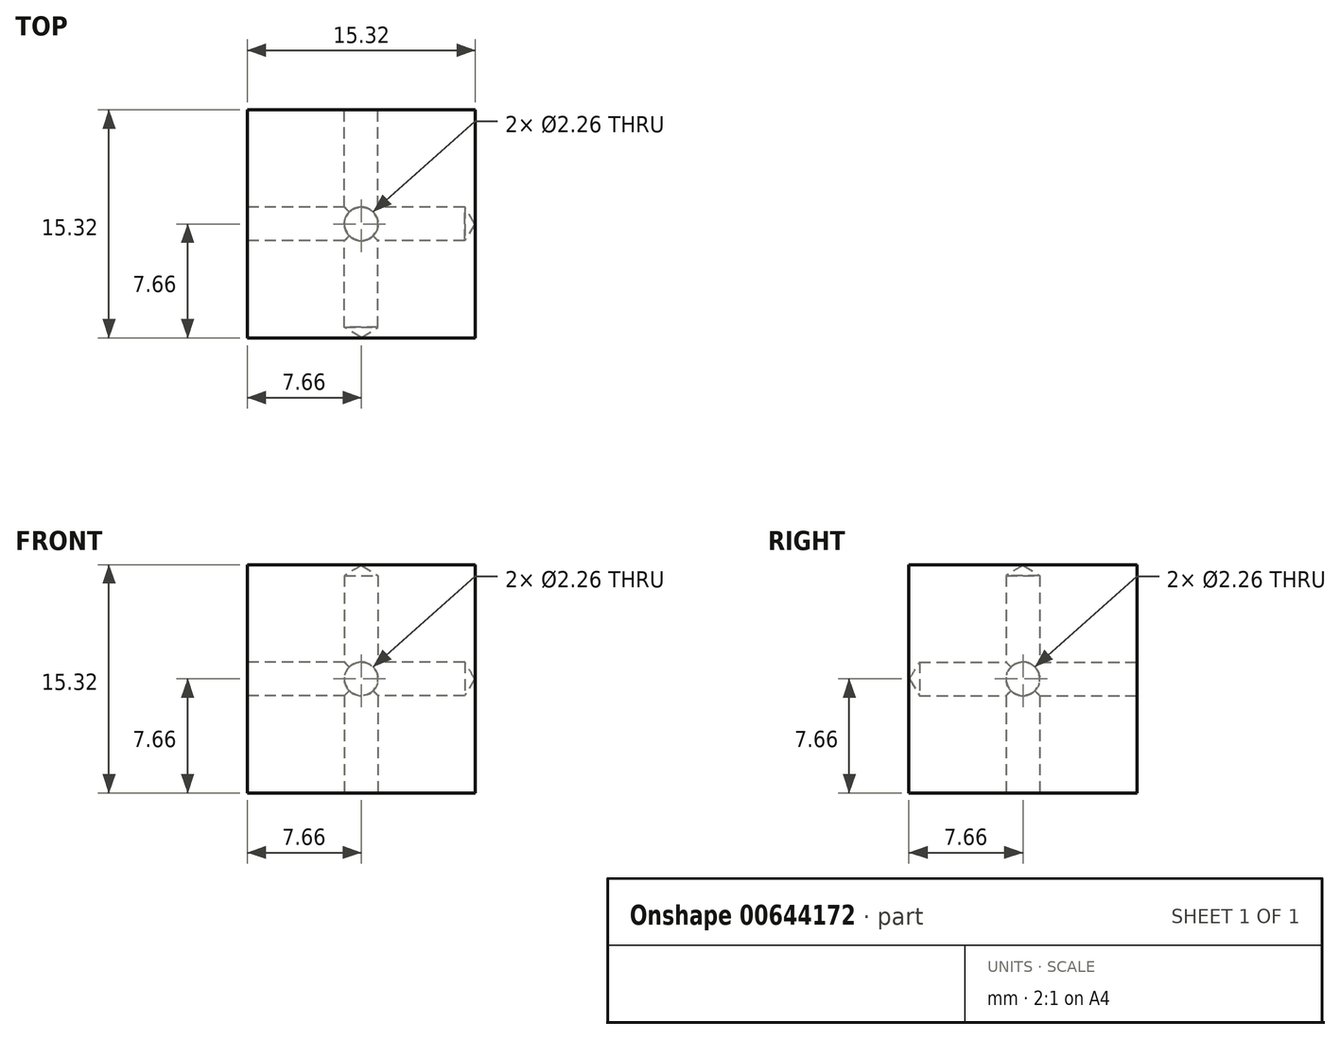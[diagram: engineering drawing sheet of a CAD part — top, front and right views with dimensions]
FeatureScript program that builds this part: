
annotation { "Feature Type Name" : "Feature", "Feature Type Description" : "" }
export const myFeature = defineFeature(function(context is Context, id is Id, definition is map)
    precondition{}
    {
        {
            var Q0;
            Q0=qCreatedBy(makeId("Top.planeOp"),FACE);
            var sketch = newSketch(context, id + "F0", { "sketchPlane" : qUnion([Q0])});
            skLineSegment(sketch, "E0.bottom", {"start": v(7.66, -7.66) * mm, "end": v(-7.66, -7.66) * mm});
            skLineSegment(sketch, "E0.top", {"start": v(7.66, 7.66) * mm, "end": v(-7.66, 7.66) * mm});
            skLineSegment(sketch, "E0.left", {"start": v(7.66, -7.66) * mm, "end": v(7.66, 7.66) * mm});
            skLineSegment(sketch, "E0.right", {"start": v(-7.66, -7.66) * mm, "end": v(-7.66, 7.66) * mm});
            skPoint(sketch, "E0.middle", {"position": v(0, 0) * mm});
            skSolve(sketch);
        }
        {
            var Q0;
            Q0 = qSketchRegion(id + "F0", true);
            extrude(context, id + "F1", {"entities" : qUnion([Q0]), "depth" : 7.66 * mm, "offsetDistance" : 25.4 * mm, "hasSecondDirection" : true, "secondDirectionOppositeDirection" : true, "secondDirectionDepth" : 7.66 * mm});
        }
        {
            var Q0;
            Q0=makeQuery(id+"F1.opExtrude","SWEPT_FACE",FACE,{"disambiguationData":[OSD([sQuery(id+"F0.wireOp",EDGE,"E0.top")])]});
            var sketch = newSketch(context, id + "F2", { "sketchPlane" : qUnion([Q0])});
            skPoint(sketch, "E1", {"position": v(0, 0) * mm});
            skSolve(sketch);
        }
        {
            var Q0;
            Q0=sQuery(id+"F2.wireOp",VERTEX,"E1");
            var Q1;
            Q1=makeQuery(id+"F1.opExtrude","SWEPT_BODY",BODY,{"disambiguationData":[OSD([sQuery(id+"F0.wireOp",EDGE,"E0.bottom"),sQuery(id+"F0.wireOp",EDGE,"E0.top"),sQuery(id+"F0.wireOp",EDGE,"E0.left"),sQuery(id+"F0.wireOp",EDGE,"E0.right")])]});
            hole(context, id + "F3", {"style" : HoleStyle.SIMPLE, "endStyle" : HoleEndStyle.BLIND, "standardTappedOrClearance" : lookupTablePath({ "standard" : "ANSI", "engagement" : "75%", "pitch" : "40 tpi", "size" : "#4", "type" : "Tapped" }), "standardBlindInLast" : lookupTablePath({ "standard" : "ANSI", "engagement" : "75%", "pitch" : "40 tpi", "size" : "#4", "type" : "Tapped" }), "holeDiameter" : 2.26 * mm, "majorDiameter" : 2.84 * mm, "showTappedDepth" : true, "holeDepth" : 14.6 * mm, "isTappedThrough" : true, "tappedDepth" : 12.7 * mm, "tapClearance" : 3, "locations" : qUnion([Q0]), "scope" : qUnion([Q1])});
        }
        {
            var Q0;
            Q0=makeQuery(id+"F1.opExtrude","CAP_FACE",FACE,{"disambiguationData":[OSD([sQuery(id+"F0.wireOp",EDGE,"E0.bottom"),sQuery(id+"F0.wireOp",EDGE,"E0.top"),sQuery(id+"F0.wireOp",EDGE,"E0.left"),sQuery(id+"F0.wireOp",EDGE,"E0.right")])],"isStart":true});
            var sketch = newSketch(context, id + "F4", { "sketchPlane" : qUnion([Q0])});
            skPoint(sketch, "E2", {"position": v(0, 0) * mm});
            skSolve(sketch);
        }
        {
            var Q0;
            Q0=sQuery(id+"F4.wireOp",VERTEX,"E2");
            var Q1;
            Q1=makeQuery(id+"F1.opExtrude","SWEPT_BODY",BODY,{"disambiguationData":[OSD([sQuery(id+"F0.wireOp",EDGE,"E0.bottom"),sQuery(id+"F0.wireOp",EDGE,"E0.top"),sQuery(id+"F0.wireOp",EDGE,"E0.left"),sQuery(id+"F0.wireOp",EDGE,"E0.right")])]});
            hole(context, id + "F5", {"style" : HoleStyle.SIMPLE, "endStyle" : HoleEndStyle.BLIND, "standardTappedOrClearance" : lookupTablePath({ "standard" : "ANSI", "engagement" : "75%", "pitch" : "40 tpi", "size" : "#4", "type" : "Tapped" }), "standardBlindInLast" : lookupTablePath({ "standard" : "ANSI", "engagement" : "75%", "pitch" : "40 tpi", "size" : "#4", "type" : "Tapped" }), "holeDiameter" : 2.26 * mm, "majorDiameter" : 2.84 * mm, "showTappedDepth" : true, "holeDepth" : 14.6 * mm, "isTappedThrough" : true, "tappedDepth" : 12.7 * mm, "tapClearance" : 3, "locations" : qUnion([Q0]), "scope" : qUnion([Q1])});
        }
        {
            var Q0;
            Q0=makeQuery(id+"F1.opExtrude","SWEPT_FACE",FACE,{"disambiguationData":[OSD([sQuery(id+"F0.wireOp",EDGE,"E0.right")])]});
            var sketch = newSketch(context, id + "F6", { "sketchPlane" : qUnion([Q0])});
            skPoint(sketch, "E3", {"position": v(0, 0) * mm});
            skSolve(sketch);
        }
        {
            var Q0;
            Q0=sQuery(id+"F6.wireOp",VERTEX,"E3");
            var Q1;
            Q1=makeQuery(id+"F1.opExtrude","SWEPT_BODY",BODY,{"disambiguationData":[OSD([sQuery(id+"F0.wireOp",EDGE,"E0.bottom"),sQuery(id+"F0.wireOp",EDGE,"E0.top"),sQuery(id+"F0.wireOp",EDGE,"E0.left"),sQuery(id+"F0.wireOp",EDGE,"E0.right")])]});
            hole(context, id + "F7", {"style" : HoleStyle.SIMPLE, "endStyle" : HoleEndStyle.BLIND, "standardTappedOrClearance" : lookupTablePath({ "standard" : "ANSI", "engagement" : "75%", "pitch" : "40 tpi", "size" : "#4", "type" : "Tapped" }), "standardBlindInLast" : lookupTablePath({ "standard" : "ANSI", "engagement" : "75%", "pitch" : "40 tpi", "size" : "#4", "type" : "Tapped" }), "holeDiameter" : 2.26 * mm, "majorDiameter" : 2.84 * mm, "showTappedDepth" : true, "holeDepth" : 14.6 * mm, "isTappedThrough" : true, "tappedDepth" : 12.7 * mm, "tapClearance" : 3, "locations" : qUnion([Q0]), "scope" : qUnion([Q1])});
        }
    });
